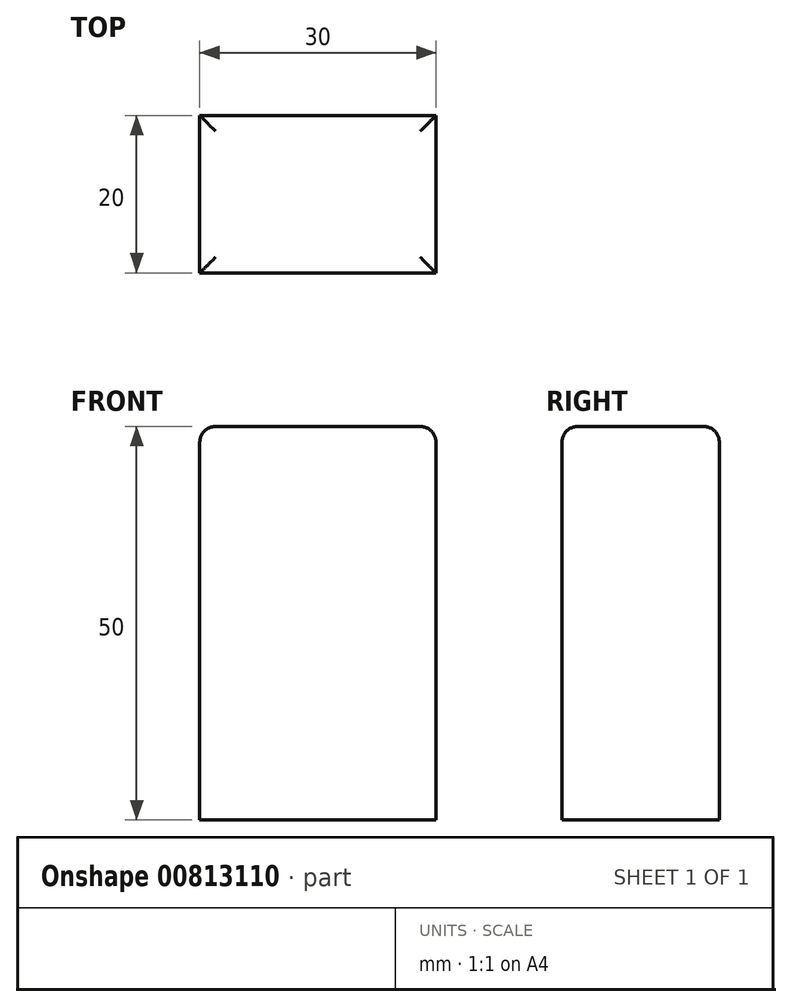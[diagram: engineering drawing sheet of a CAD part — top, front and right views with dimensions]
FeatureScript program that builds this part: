
annotation { "Feature Type Name" : "Feature", "Feature Type Description" : "" }
export const myFeature = defineFeature(function(context is Context, id is Id, definition is map)
    precondition{}
    {
        {
            var Q0;
            Q0=qCreatedBy(makeId("Top.planeOp"),FACE);
            var sketch = newSketch(context, id + "F0", { "sketchPlane" : qUnion([Q0])});
            skLineSegment(sketch, "E0.bottom", {"start": v(15, -10) * mm, "end": v(-15, -10) * mm});
            skLineSegment(sketch, "E0.top", {"start": v(15, 10) * mm, "end": v(-15, 10) * mm});
            skLineSegment(sketch, "E0.left", {"start": v(15, -10) * mm, "end": v(15, 10) * mm});
            skLineSegment(sketch, "E0.right", {"start": v(-15, -10) * mm, "end": v(-15, 10) * mm});
            skPoint(sketch, "E0.middle", {"position": v(0, 0) * mm});
            skSolve(sketch);
        }
        {
            var Q0;
            Q0 = qSketchRegion(id + "F0", true);
            extrude(context, id + "F1", {"entities" : qUnion([Q0]), "depth" : 50 * mm, "offsetDistance" : 25 * mm});
        }
        {
            var Q0;
            Q0=makeQuery(id+"F1.opExtrude","CAP_EDGE",EDGE,{"disambiguationData":[OSD([sQuery(id+"F0.wireOp",EDGE,"E0.bottom")])],"isStart":false});
            var Q1;
            Q1=makeQuery(id+"F1.opExtrude","CAP_EDGE",EDGE,{"disambiguationData":[OSD([sQuery(id+"F0.wireOp",EDGE,"E0.left")])],"isStart":false});
            var Q2;
            Q2=makeQuery(id+"F1.opExtrude","CAP_EDGE",EDGE,{"disambiguationData":[OSD([sQuery(id+"F0.wireOp",EDGE,"E0.top")])],"isStart":false});
            var Q3;
            Q3=makeQuery(id+"F1.opExtrude","CAP_EDGE",EDGE,{"disambiguationData":[OSD([sQuery(id+"F0.wireOp",EDGE,"E0.right")])],"isStart":false});
            fillet(context, id + "F2", {"entities" : qUnion([Q0, Q1, Q2, Q3]), "radius" : 2 * mm, "tangentPropagation" : true, "allowEdgeOverflow" : false});
        }
    });
